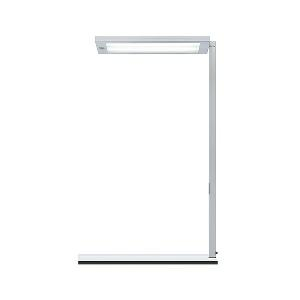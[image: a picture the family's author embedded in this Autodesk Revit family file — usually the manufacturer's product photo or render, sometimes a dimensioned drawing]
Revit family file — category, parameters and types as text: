
# Revit family: lavigo_-_dpt_6000_840_r_g2_00804456_e6c9
name_source: partatom
category: Lighting Fixtures
units: mm (PartAtom-declared; Revit-internal decimal feet)

## family parameters
Cut with Voids When Loaded = No
Host = Face
Light Source = No
Part Type = Normal
Room Calculation Point = No
Round Connector Dimension = Use Diameter
Shared = No

## types (1)
- LAVIGO - DPT 6000/840/R/G2 (1 x LED, 5950 lm, 4000K)
    Apparent Load = 45 VA
    Approval mark = CE
    CIE Flux Codes = 60 87 97 29 100
    Color Rendering = 80-89
    Color Temperature = 4000K
    Control Gear = Electronic ballast
    Default Elevation = 1800 mm
    Description = DPT 6000/840/R/G2|Desk-mounted luminaire|light source: LED|work equipment: Electronic ballast|connected load: 220-240 V, 50/60 Hz|Power consumption: approx. 45 W|standby: approx. 0,50|power factor: approx. 0,865|luminous flux: 5950 lm|luminous efficacy: 132 lm/W|light distribution: Direct/indirect|direct ratio: approx. 29 %|colour temperature: Cold white, ca. 4000 K|color rendering index (CRI): >= 80|chromaticity tolerance:  3 SDCM|technology: Presence and daylight sensor control (PIR)|operation: Multi-function switch|luminaire body|material: Steel/plastic|surface: Painted|colour: White|lamp cover: Acrylic (PMMA), Satine|tubular section|material: Steel tube|surface: Painted|Form: Tubular section upright|colour of tubular section: White|weight (net): approx. 9.5 kg|mains lead: 3.70 m Mains plug CEE 7/VII|Fastening: Socket, Table adaptor|decorative contrast side parts: Flint grey|glare control: Prism aperture|luminance(L65): <= 3000 cd/m|unified glare rating(4H 8H): <=  16|special features: Luminaire head detachable, Cradle to Cradle Certified TM, Direct light component with edge light and light-guide technology for homogenous light exit, Flicker-free, Integrated light and presence sensor PIR, Retrofittable with TALK module, Inclination of tubular section adjustable, Separated, direct and indirect light individually adjustable|
    Frequency = 50 Hz, 60 Hz
    Height = 36 mm
    Lamp = 1 x LED
    Lamp Light Flux = 5950 lm
    Lamp count = 1
    Length = 675 mm
    Luminous efficacy = 132 lm/W
    Manufacturer = Waldmann
    ModVariant = No
    Model = 00804456
    Mounting Place = Table
    Mounting Type = Surface mounted
    Number of Poles = 1
    OnlyDefault = Yes
    Power Factor = 1
    Product Name = LAVIGO - DPT 6000/840/R/G2
    Product group = Desk mounted luminaire with detector
    ProductGroupID = 2201
    Protection Class = Protection class I
    Protection Degree = IP 20
    RLX_Detail_Level = 1
    RLX_Emergency_Light_Flux = 0 lm
    RLX_Emergency_Type = 0
    RLX_Emergency_Type_DB = No
    RlxData = <blob elided: 35889 chars, md5=9f9b828b>
    Socket = socket
    Standby Power = 0 W
    System Light Flux = 5950 lm
    System Power = 45 W
    Type Comments = Product without accessories
    Type Image = 121716000-00630762.jpg
    URL = http://relux.com
    VarID = ---
    Voltage = 230 V
    Voltage Range = 220-240 V
    Weight = 0.00 kg
    Width = 320 mm

## geometry (parser evidence)
native form markers: Blend x4, Sweep x17
no freeform markers — native parametric forms only
